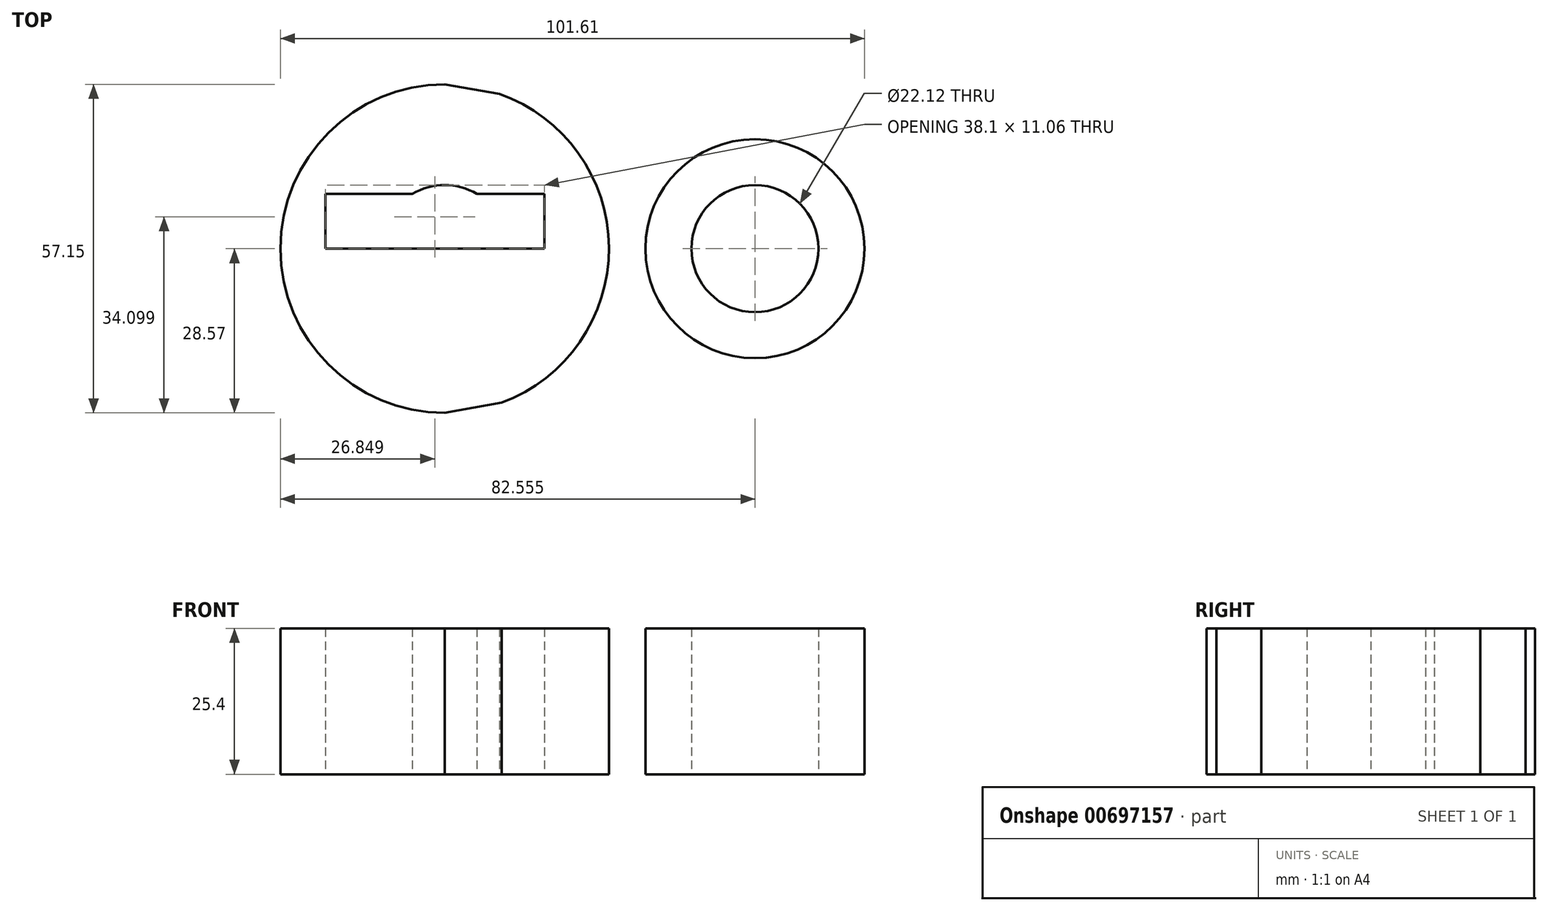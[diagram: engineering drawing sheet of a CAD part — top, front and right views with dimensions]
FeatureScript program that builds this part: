
annotation { "Feature Type Name" : "Feature", "Feature Type Description" : "" }
export const myFeature = defineFeature(function(context is Context, id is Id, definition is map)
    precondition{}
    {
        {
            var Q0;
            Q0=qCreatedBy(makeId("Top.planeOp"),FACE);
            var sketch = newSketch(context, id + "F0", { "sketchPlane" : qUnion([Q0])});
            skCircle(sketch, "E0", {"center": v(0, 0) * mm, "radius": 28.58 * mm});
            skCircle(sketch, "E1", {"center": v(53.98, 0) * mm, "radius": 19.05 * mm});
            skLineSegment(sketch, "E2", {"start": v(0, 28.58) * mm, "end": v(57.2, 18.78) * mm});
            skLineSegment(sketch, "E3", {"start": v(0, -28.58) * mm, "end": v(53.34, -19.04) * mm});
            skCircle(sketch, "E4", {"center": v(0, 0) * mm, "radius": 11.06 * mm});
            skCircle(sketch, "E5", {"center": v(53.98, 0) * mm, "radius": 11.06 * mm});
            skLineSegment(sketch, "E6.bottom", {"start": v(17.32, 0) * mm, "end": v(-20.78, 0) * mm});
            skLineSegment(sketch, "E6.top", {"start": v(17.32, 9.53) * mm, "end": v(-20.78, 9.52) * mm});
            skLineSegment(sketch, "E6.left", {"start": v(17.32, 0) * mm, "end": v(17.32, 9.53) * mm});
            skLineSegment(sketch, "E6.right", {"start": v(-20.78, 0) * mm, "end": v(-20.78, 9.52) * mm});
            skSolve(sketch);
        }
        {
            var Q0;
            {var subQ0=sQuery(id+"F0.wireOp",EDGE,"E2");var subQ1=sQuery(id+"F0.wireOp",EDGE,"E0");var subQ2=makeQuery(id+"F0.imprint","INTERSECT",VERTEX,{"disambiguationData":[OD(0.0)],"derivedFrom":[subQ1,subQ0]});Q0=makeQuery(id+"F0.imprint","IMPRINT",FACE,{"disambiguationData":[TD([[makeQuery(id+"F0.imprint","IMPRINT",EDGE,{"disambiguationData":[TD([[subQ2,1.0]])],"derivedFrom":subQ1}),1.0]])]});}
            var Q1;
            {var subQ0=sQuery(id+"F0.wireOp",EDGE,"E3");var subQ1=sQuery(id+"F0.wireOp",EDGE,"E0");var subQ2=makeQuery(id+"F0.imprint","INTERSECT",VERTEX,{"disambiguationData":[OD(0.0)],"derivedFrom":[subQ1,subQ0]});Q1=makeQuery(id+"F0.imprint","IMPRINT",FACE,{"disambiguationData":[TD([[makeQuery(id+"F0.imprint","IMPRINT",EDGE,{"disambiguationData":[TD([[subQ2,-1.0]])],"derivedFrom":subQ1}),1.0]])]});}
            var Q2;
            {var subQ0=sQuery(id+"F0.wireOp",EDGE,"E2");var subQ1=sQuery(id+"F0.wireOp",EDGE,"E0");var subQ2=makeQuery(id+"F0.imprint","INTERSECT",VERTEX,{"disambiguationData":[OD(1.0)],"derivedFrom":[subQ1,subQ0]});Q2=makeQuery(id+"F0.imprint","IMPRINT",FACE,{"disambiguationData":[TD([[makeQuery(id+"F0.imprint","IMPRINT",EDGE,{"disambiguationData":[TD([[subQ2,1.0]])],"derivedFrom":subQ1}),-1.0]])]});}
            var Q3;
            Q3=makeQuery(id+"F0.imprint","IMPRINT",FACE,{"disambiguationData":[TD([[makeQuery(id+"F0.imprint","IMPRINT",EDGE,{"derivedFrom":sQuery(id+"F0.wireOp",EDGE,"E5")}),-1.0]])]});
            var Q4;
            {var subQ4=sQuery(id+"F0.wireOp",EDGE,"E6.left");Q4=makeQuery(id+"F0.imprint","IMPRINT",FACE,{"disambiguationData":[TD([[makeQuery(id+"F0.imprint","IMPRINT",EDGE,{"derivedFrom":subQ4}),-1.0]])]});}
            var Q5;
            {var subQ0=sQuery(id+"F0.wireOp",EDGE,"E6.bottom");var subQ1=sQuery(id+"F0.wireOp",EDGE,"E4");var subQ2=makeQuery(id+"F0.imprint","INTERSECT",VERTEX,{"disambiguationData":[OD(0.0)],"derivedFrom":[subQ1,subQ0]});Q5=makeQuery(id+"F0.imprint","IMPRINT",FACE,{"disambiguationData":[TD([[makeQuery(id+"F0.imprint","IMPRINT",EDGE,{"disambiguationData":[TD([[subQ2,1.0]])],"derivedFrom":subQ1}),1.0]])]});}
            extrude(context, id + "F1", {"entities" : qUnion([Q0, Q1, Q2, Q3, Q4, Q5]), "depth" : 25.4 * mm, "offsetDistance" : 25.4 * mm});
        }
    });
